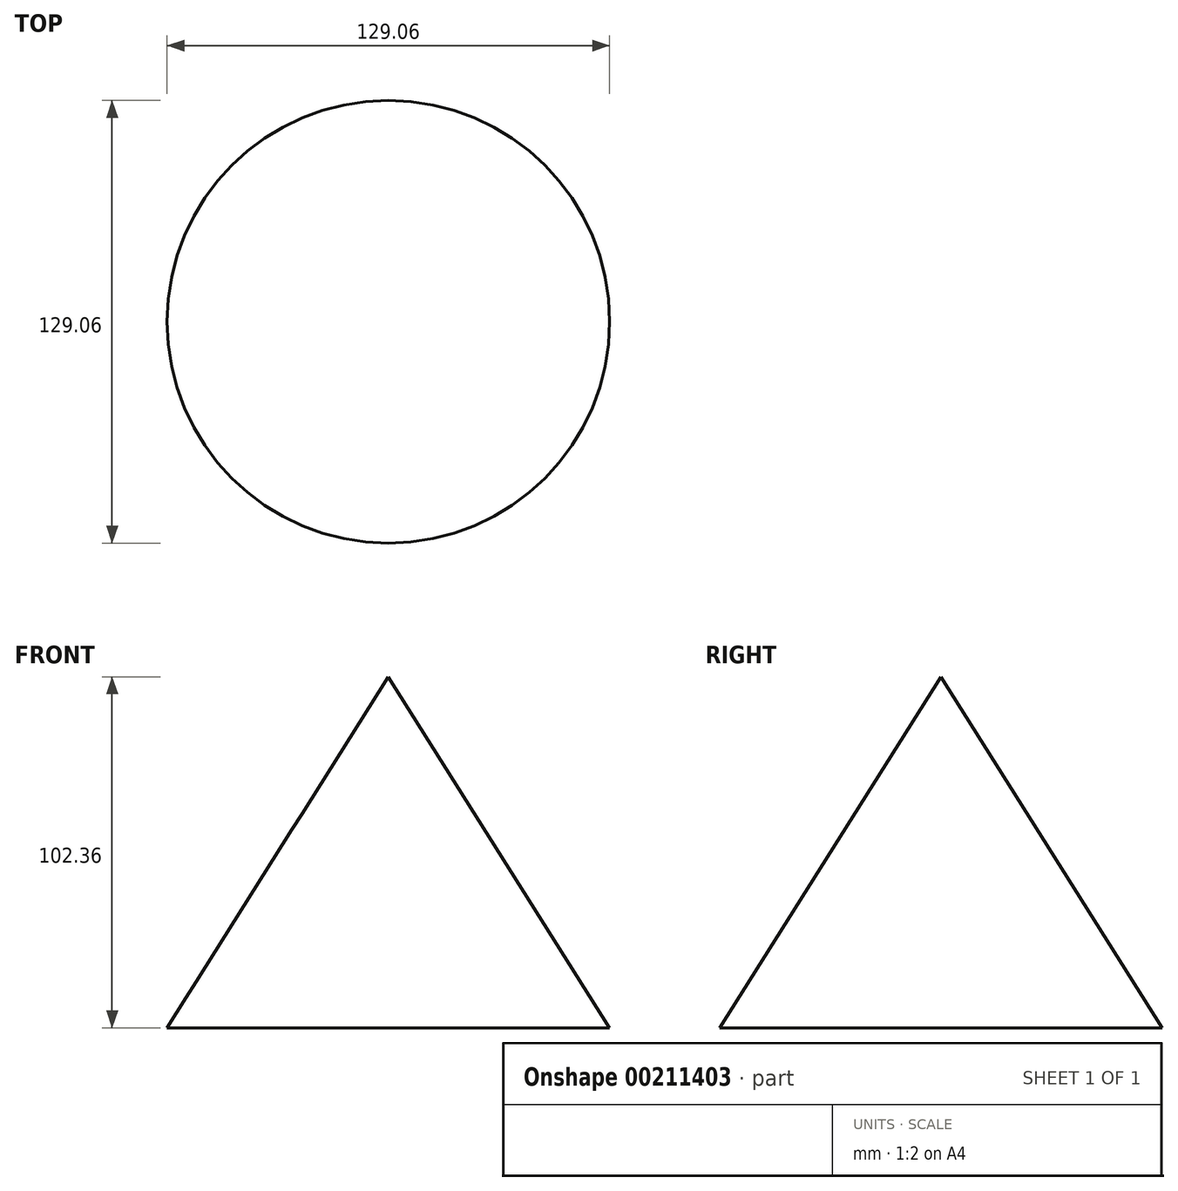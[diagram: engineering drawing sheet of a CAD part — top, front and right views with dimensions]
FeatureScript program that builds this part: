
annotation { "Feature Type Name" : "Feature", "Feature Type Description" : "" }
export const myFeature = defineFeature(function(context is Context, id is Id, definition is map)
    precondition{}
    {
        {
            var Q0;
            Q0=qCreatedBy(makeId("Front.planeOp"),FACE);
            var sketch = newSketch(context, id + "F0", { "sketchPlane" : qUnion([Q0])});
            skLineSegment(sketch, "E0", {"start": v(0, 48.54) * mm, "end": v(0, -53.82) * mm});
            skLineSegment(sketch, "E1", {"start": v(0, -53.82) * mm, "end": v(64.53, -53.82) * mm});
            skLineSegment(sketch, "E2", {"start": v(0, 48.54) * mm, "end": v(64.53, -53.82) * mm});
            skSolve(sketch);
        }
        {
            var Q0;
            Q0=makeQuery(id+"F0.imprint","IMPRINT",FACE,{"disambiguationData":[TD([[makeQuery(id+"F0.imprint","IMPRINT",EDGE,{"derivedFrom":sQuery(id+"F0.wireOp",EDGE,"E0")}),1.0]])]});
            var Q1;
            Q1=sQuery(id+"F0.wireOp",EDGE,"E0");
            var Q2;
            Q2=sQuery(id+"F0.wireOp",EDGE,"E0");
            revolve(context, id + "F1", {"entities" : qUnion([Q0]), "surfaceEntities" : qUnion([Q1]), "axis" : qUnion([Q2]), "revolveType" : RevolveType.FULL});
        }
    });
